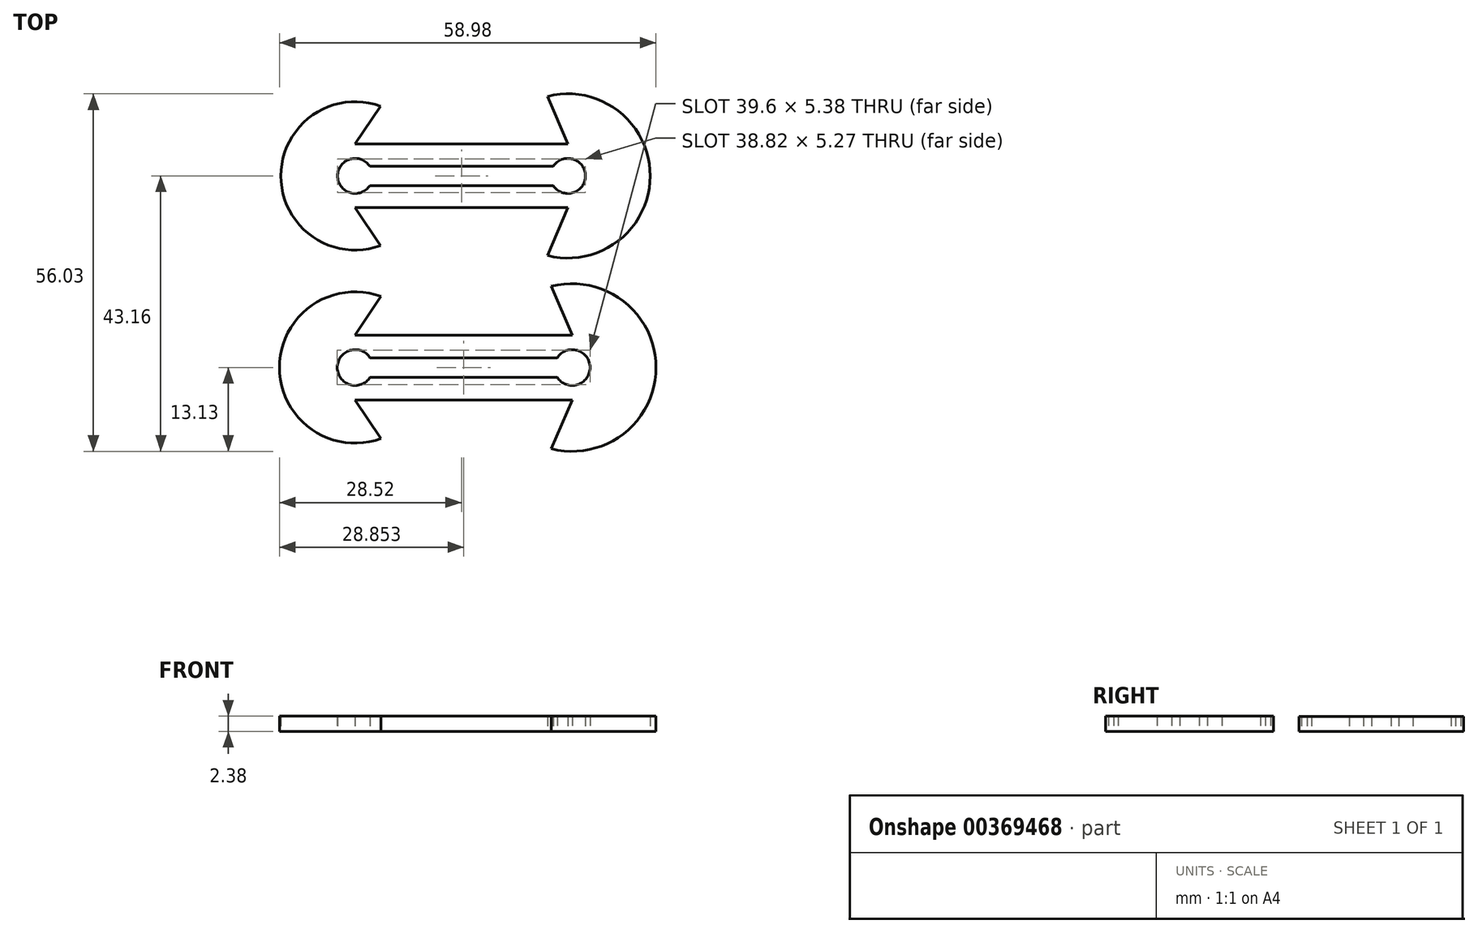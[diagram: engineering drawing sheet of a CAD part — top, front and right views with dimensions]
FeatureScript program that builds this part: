
annotation { "Feature Type Name" : "Feature", "Feature Type Description" : "" }
export const myFeature = defineFeature(function(context is Context, id is Id, definition is map)
    precondition{}
    {
        {
            var Q0;
            Q0=qCreatedBy(makeId("Top.planeOp"),FACE);
            var sketch = newSketch(context, id + "F0", { "sketchPlane" : qUnion([Q0])});
            skArc(sketch, "E0", {"start": v(3.98, 10.92) * mm, "mid": v(-11.62, 0) * mm, "end": v(3.98, -10.92) * mm});
            skArc(sketch, "E1", {"start": v(30.12, -12.47) * mm, "mid": v(46.2, 0) * mm, "end": v(30.12, 12.47) * mm});
            skPoint(sketch, "E2.orphan", {"position": v(0, 4.36) * mm});
            skLineSegment(sketch, "E3.top", {"start": v(0, 4.98) * mm, "end": v(33.32, 4.98) * mm});
            skLineSegment(sketch, "E3.left", {"start": v(0, 0) * mm, "end": v(0, 4.98) * mm});
            skLineSegment(sketch, "E3.right", {"start": v(33.32, 0) * mm, "end": v(33.32, 4.98) * mm});
            skLineSegment(sketch, "E4.MirrorCS", {"start": v(0, -4.98) * mm, "end": v(33.32, -4.98) * mm});
            skLineSegment(sketch, "E5", {"start": v(33.32, 0) * mm, "end": v(33.32, -4.98) * mm});
            skLineSegment(sketch, "E6", {"start": v(33.32, 4.98) * mm, "end": v(33.32, -4.98) * mm});
            skLineSegment(sketch, "E7.top", {"start": v(0, 1.5) * mm, "end": v(33.32, 1.5) * mm});
            skLineSegment(sketch, "E7.left", {"start": v(0, 0) * mm, "end": v(0, 1.5) * mm});
            skLineSegment(sketch, "E7.right", {"start": v(33.32, 0) * mm, "end": v(33.32, 1.5) * mm});
            skLineSegment(sketch, "E8.MirrorCS", {"start": v(0, -1.5) * mm, "end": v(33.32, -1.5) * mm});
            skPoint(sketch, "E9.orphan", {"position": v(0, 11.62) * mm});
            skLineSegment(sketch, "E10", {"start": v(3.98, 10.92) * mm, "end": v(0, 4.98) * mm});
            skLineSegment(sketch, "E11", {"start": v(3.98, -10.92) * mm, "end": v(0, -4.98) * mm});
            skPoint(sketch, "E12.orphan", {"position": v(30.12, -12.47) * mm});
            skLineSegment(sketch, "E13", {"start": v(30.12, 12.47) * mm, "end": v(33.32, 4.98) * mm});
            skLineSegment(sketch, "E14", {"start": v(30.12, -12.47) * mm, "end": v(33.32, -4.98) * mm});
            skPoint(sketch, "E15.orphan", {"position": v(33.32, 12.88) * mm});
            skLineSegment(sketch, "E16", {"start": v(0, -1.5) * mm, "end": v(0, 1.5) * mm});
            skSolve(sketch);
        }
        {
            var Q0;
            Q0 = qSketchRegion(id + "F0", true);
            extrude(context, id + "F1", {"entities" : qUnion([Q0]), "depth" : 2.33 * mm});
        }
        {
            var Q0;
            Q0=sQuery(id+"F0.wireOp",VERTEX,"E3.left.start");
            var Q1;
            Q1=sQuery(id+"F0.wireOp",VERTEX,"E5.start");
            var Q2;
            Q2=makeQuery(id+"F1.opExtrude","SWEPT_BODY",BODY,{"disambiguationData":[OSD([sQuery(id+"F0.wireOp",EDGE,"E0"),sQuery(id+"F0.wireOp",EDGE,"E1"),sQuery(id+"F0.wireOp",EDGE,"E3.top"),sQuery(id+"F0.wireOp",EDGE,"E4.MirrorCS"),sQuery(id+"F0.wireOp",EDGE,"kJXo7HvB-q0wJ-KMkF-qbSK-HqD1jnp9HCBe"),sQuery(id+"F0.wireOp",EDGE,"E6")])]});
            hole(context, id + "F2", {"style" : HoleStyle.SIMPLE, "endStyle" : HoleEndStyle.THROUGH, "oppositeDirection" : true, "standardTappedOrClearance" : lookupTablePath({ "standard" : "ISO", "fit" : "Normal", "size" : "M5", "type" : "Clearance" }), "standardBlindInLast" : lookupTablePath({ "fit" : "Standard", "standard" : "ISO", "size" : "M5", "type" : "Clearance" }), "holeDiameter" : 5.5 * mm, "isTappedThrough" : true, "tappedDepth" : 12 * mm, "tapClearance" : 3, "locations" : qUnion([Q0, Q1]), "scope" : qUnion([Q2])});
        }
        {
            var Q0;
            Q0=makeQuery(id+"F1.opExtrude","SWEPT_BODY",BODY,{"disambiguationData":[OSD([sQuery(id+"F0.wireOp",EDGE,"E0"),sQuery(id+"F0.wireOp",EDGE,"E1"),sQuery(id+"F0.wireOp",EDGE,"E3.top"),sQuery(id+"F0.wireOp",EDGE,"E4.MirrorCS"),sQuery(id+"F0.wireOp",EDGE,"kJXo7HvB-q0wJ-KMkF-qbSK-HqD1jnp9HCBe"),sQuery(id+"F0.wireOp",EDGE,"E6"),sQuery(id+"F0.wireOp",EDGE,"E7.top"),sQuery(id+"F0.wireOp",EDGE,"E7.left"),sQuery(id+"F0.wireOp",EDGE,"E7.right"),sQuery(id+"F0.wireOp",EDGE,"E8.MirrorCS")])]});
            var Q1;
            Q1=sQuery(id+"F0.wireOp",VERTEX,"E7.top.start");
            transform(context, id + "F3", {"entities" : qUnion([Q0]), "transformType" : TransformType.SCALE_UNIFORMLY, "scale" : 1.02, "scalePoint" : qUnion([Q1]), "makeCopy" : true});
        }
        {
            var Q0;
            Q0=makeQuery(id+"F3.opPattern","COPY",BODY,{"derivedFrom":makeQuery(id+"F1.opExtrude","SWEPT_BODY",BODY,{"disambiguationData":[OSD([sQuery(id+"F0.wireOp",EDGE,"E0"),sQuery(id+"F0.wireOp",EDGE,"E1"),sQuery(id+"F0.wireOp",EDGE,"E3.top"),sQuery(id+"F0.wireOp",EDGE,"E4.MirrorCS"),sQuery(id+"F0.wireOp",EDGE,"kJXo7HvB-q0wJ-KMkF-qbSK-HqD1jnp9HCBe"),sQuery(id+"F0.wireOp",EDGE,"E6"),sQuery(id+"F0.wireOp",EDGE,"E7.top"),sQuery(id+"F0.wireOp",EDGE,"E7.left"),sQuery(id+"F0.wireOp",EDGE,"E7.right"),sQuery(id+"F0.wireOp",EDGE,"E8.MirrorCS")])]}),"instanceName":"1"});
            transform(context, id + "F4", {"entities" : qUnion([Q0]), "transformType" : TransformType.TRANSLATION_3D, "dx" : 0 * mm, "dy" : -30 * mm, "dz" : 0 * mm, "makeCopy" : false});
        }
    });
